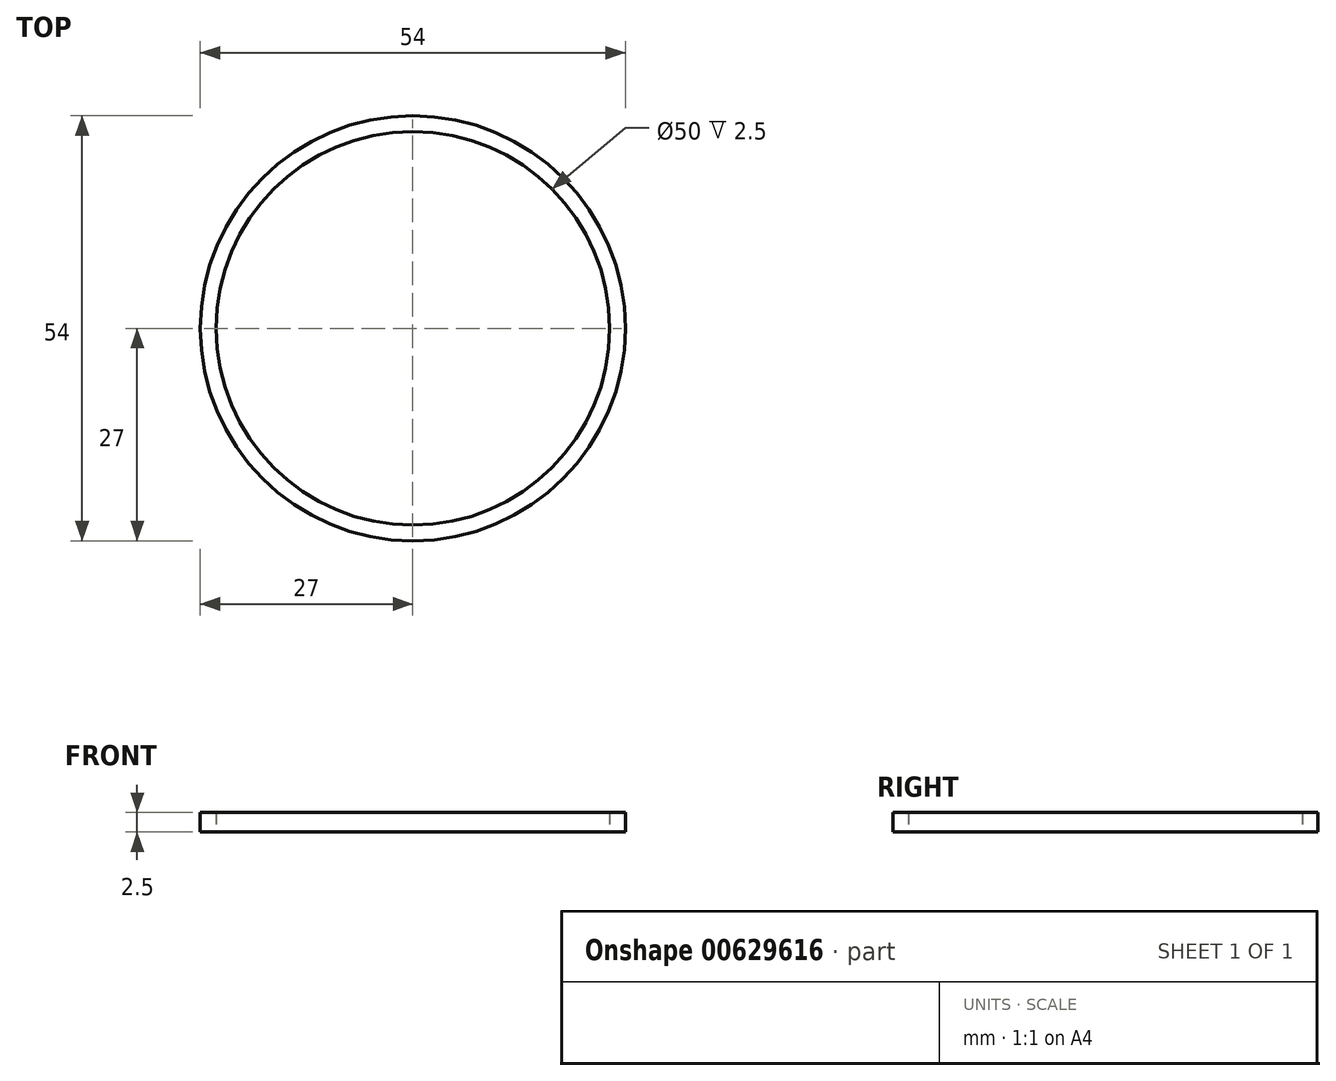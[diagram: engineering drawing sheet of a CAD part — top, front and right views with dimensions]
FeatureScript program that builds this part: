
annotation { "Feature Type Name" : "Feature", "Feature Type Description" : "" }
export const myFeature = defineFeature(function(context is Context, id is Id, definition is map)
    precondition{}
    {
        {
            var Q0;
            Q0=qCreatedBy(makeId("Top.planeOp"),FACE);
            var sketch = newSketch(context, id + "F0", { "sketchPlane" : qUnion([Q0])});
            skCircle(sketch, "E0", {"center": v(0, 0) * mm, "radius": 25 * mm});
            skCircle(sketch, "E1", {"center": v(0, 0) * mm, "radius": 27 * mm});
            skSolve(sketch);
        }
        {
            var Q0;
            Q0 = qSketchRegion(id + "F0", true);
            extrude(context, id + "F1", {"entities" : qUnion([Q0]), "depth" : 2.5 * mm, "offsetDistance" : 25 * mm});
        }
    });
